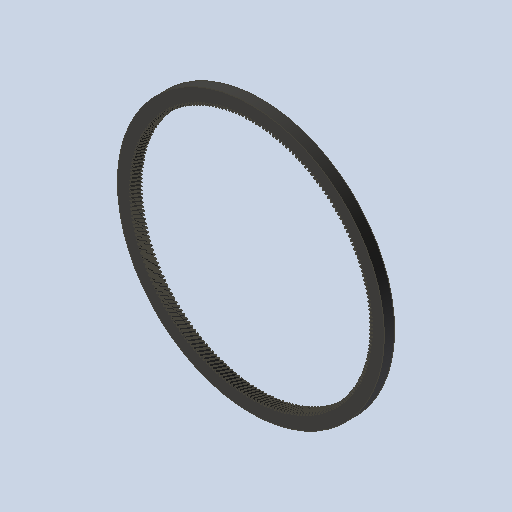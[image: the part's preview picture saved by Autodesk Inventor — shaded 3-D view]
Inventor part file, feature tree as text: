
AUTODESK INVENTOR PART (.ipt)
format: ipt  version: 2023 (Build 270158000, 158)  size: 2,446,336 bytes
history: native  units: mm (DEFAULTED — no unit token found)
features: plane x3, other x3, sketch x2, extrude x1
ambient origin geometry x8: Origin, YZ Plane, XZ Plane, XY Plane, X Axis, Y Axis, Z Axis, Center Point
bodies: Solid1 (feature_tree)
feature tree (9):
  extrude  "Extrusion1"  Depth=10.0mm TaperAngle=0.0deg
  plane  "Work Plane2"
  plane  "Work Plane8"
  plane  "Work Plane9"
  other  "Spur Gear"
  sketch  "Sketch1"  dims[d0=260.694866mm d1=10.0mm d2=0.0mm]
  sketch  "Sketch2"  dims[d3=234.11911mm d4=10.0mm d5=0.0mm d16=80.0mm d17=0.0mm d34=0.1428mm d39=0.0mm d45=0.0mm d47=80.0mm d50=0.0mm d51=0.0mm d52=80.0mm]
  other  "Srf1"
  other  "Pitch Diameter"
